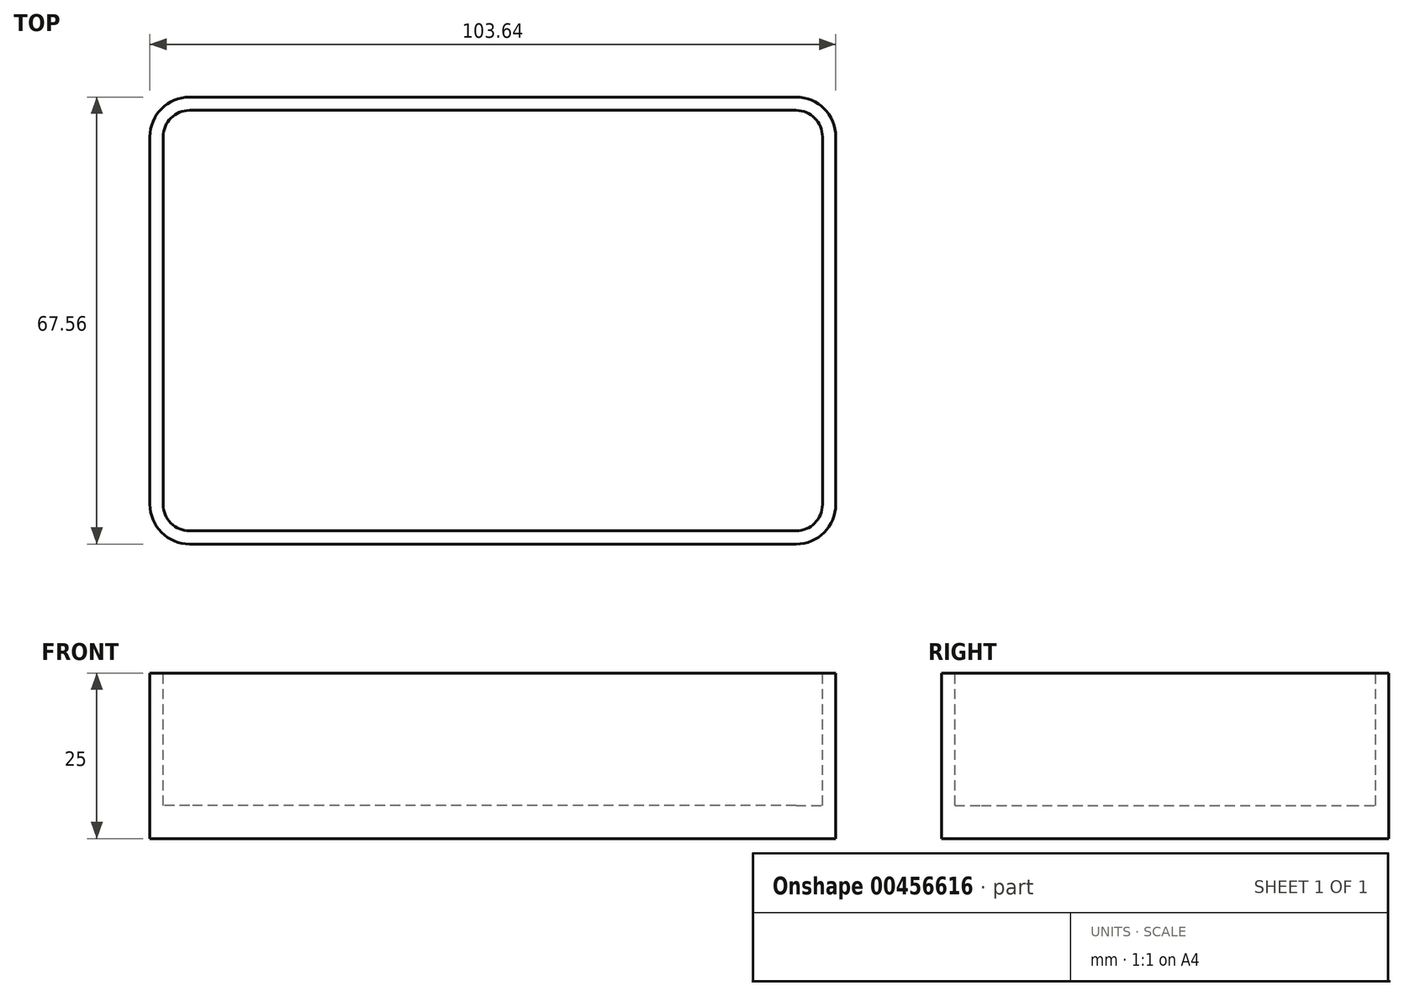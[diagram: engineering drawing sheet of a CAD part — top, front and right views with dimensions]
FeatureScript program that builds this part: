
annotation { "Feature Type Name" : "Feature", "Feature Type Description" : "" }
export const myFeature = defineFeature(function(context is Context, id is Id, definition is map)
    precondition{}
    {
        {
            var Q0;
            Q0=qCreatedBy(makeId("Top.planeOp"),FACE);
            var sketch = newSketch(context, id + "F0", { "sketchPlane" : qUnion([Q0])});
            skLineSegment(sketch, "E0.bottom", {"start": v(45.82, -33.78) * mm, "end": v(-45.82, -33.78) * mm});
            skLineSegment(sketch, "E0.top", {"start": v(45.82, 33.78) * mm, "end": v(-45.82, 33.78) * mm});
            skLineSegment(sketch, "E0.left", {"start": v(51.82, -27.78) * mm, "end": v(51.82, 27.78) * mm});
            skLineSegment(sketch, "E0.right", {"start": v(-51.82, -27.78) * mm, "end": v(-51.82, 27.78) * mm});
            skPoint(sketch, "E0.middle", {"position": v(0, 0) * mm});
            skPoint(sketch, "E1.visualSharp", {"position": v(-51.82, 33.78) * mm});
            skArc(sketch, "E1.filletArc", {"start": v(-45.82, 33.78) * mm, "mid": v(-50.06, 32.02) * mm, "end": v(-51.82, 27.78) * mm});
            skPoint(sketch, "E2.visualSharp", {"position": v(51.82, 33.78) * mm});
            skArc(sketch, "E2.filletArc", {"start": v(51.82, 27.78) * mm, "mid": v(50.06, 32.02) * mm, "end": v(45.82, 33.78) * mm});
            skPoint(sketch, "E3.visualSharp", {"position": v(51.82, -33.78) * mm});
            skArc(sketch, "E3.filletArc", {"start": v(45.82, -33.78) * mm, "mid": v(50.06, -32.02) * mm, "end": v(51.82, -27.78) * mm});
            skPoint(sketch, "E4.visualSharp", {"position": v(-51.82, -33.78) * mm});
            skArc(sketch, "E4.filletArc", {"start": v(-51.82, -27.78) * mm, "mid": v(-50.06, -32.02) * mm, "end": v(-45.82, -33.78) * mm});
            skSolve(sketch);
        }
        {
            var Q0;
            Q0=makeQuery(id+"F0.imprint","IMPRINT",FACE,{"disambiguationData":[TD([[makeQuery(id+"F0.imprint","IMPRINT",EDGE,{"derivedFrom":sQuery(id+"F0.wireOp",EDGE,"E0.bottom")}),-1.0]])]});
            extrude(context, id + "F1", {"entities" : qUnion([Q0]), "depth" : 25 * mm});
        }
        {
            var Q0;
            Q0=makeQuery(id+"F1.opExtrude","CAP_FACE",FACE,{"disambiguationData":[OSD([sQuery(id+"F0.wireOp",EDGE,"E0.bottom"),sQuery(id+"F0.wireOp",EDGE,"E0.top"),sQuery(id+"F0.wireOp",EDGE,"E0.left"),sQuery(id+"F0.wireOp",EDGE,"E0.right"),sQuery(id+"F0.wireOp",EDGE,"E1.filletArc"),sQuery(id+"F0.wireOp",EDGE,"E2.filletArc"),sQuery(id+"F0.wireOp",EDGE,"E3.filletArc"),sQuery(id+"F0.wireOp",EDGE,"E4.filletArc")])],"isStart":false});
            var sketch = newSketch(context, id + "F2", { "sketchPlane" : qUnion([Q0])});
            skLineSegment(sketch, "E5.0", {"start": v(49.82, -27.78) * mm, "end": v(49.82, 27.78) * mm});
            skArc(sketch, "E5.1", {"start": v(45.82, -31.78) * mm, "mid": v(48.64, -30.61) * mm, "end": v(49.82, -27.78) * mm});
            skArc(sketch, "E5.2", {"start": v(49.82, 27.78) * mm, "mid": v(48.64, 30.61) * mm, "end": v(45.82, 31.78) * mm});
            skLineSegment(sketch, "E5.3", {"start": v(-45.82, -31.78) * mm, "end": v(45.82, -31.78) * mm});
            skLineSegment(sketch, "E5.4", {"start": v(45.82, 31.78) * mm, "end": v(-45.82, 31.78) * mm});
            skArc(sketch, "E5.5", {"start": v(-45.82, 31.78) * mm, "mid": v(-48.64, 30.61) * mm, "end": v(-49.82, 27.78) * mm});
            skLineSegment(sketch, "E5.6", {"start": v(-49.82, 27.78) * mm, "end": v(-49.82, -27.78) * mm});
            skArc(sketch, "E5.7", {"start": v(-49.82, -27.78) * mm, "mid": v(-48.64, -30.61) * mm, "end": v(-45.82, -31.78) * mm});
            skSolve(sketch);
        }
        {
            var Q0;
            Q0=makeQuery(id+"F2.imprint","IMPRINT",FACE,{"disambiguationData":[TD([[makeQuery(id+"F2.imprint","IMPRINT",EDGE,{"derivedFrom":sQuery(id+"F2.wireOp",EDGE,"E5.0")}),1.0]])]});
            extrude(context, id + "F3", {"entities" : qUnion([Q0]), "operationType" : NewBodyOperationType.REMOVE, "oppositeDirection" : true, "depth" : 20 * mm});
        }
    });
